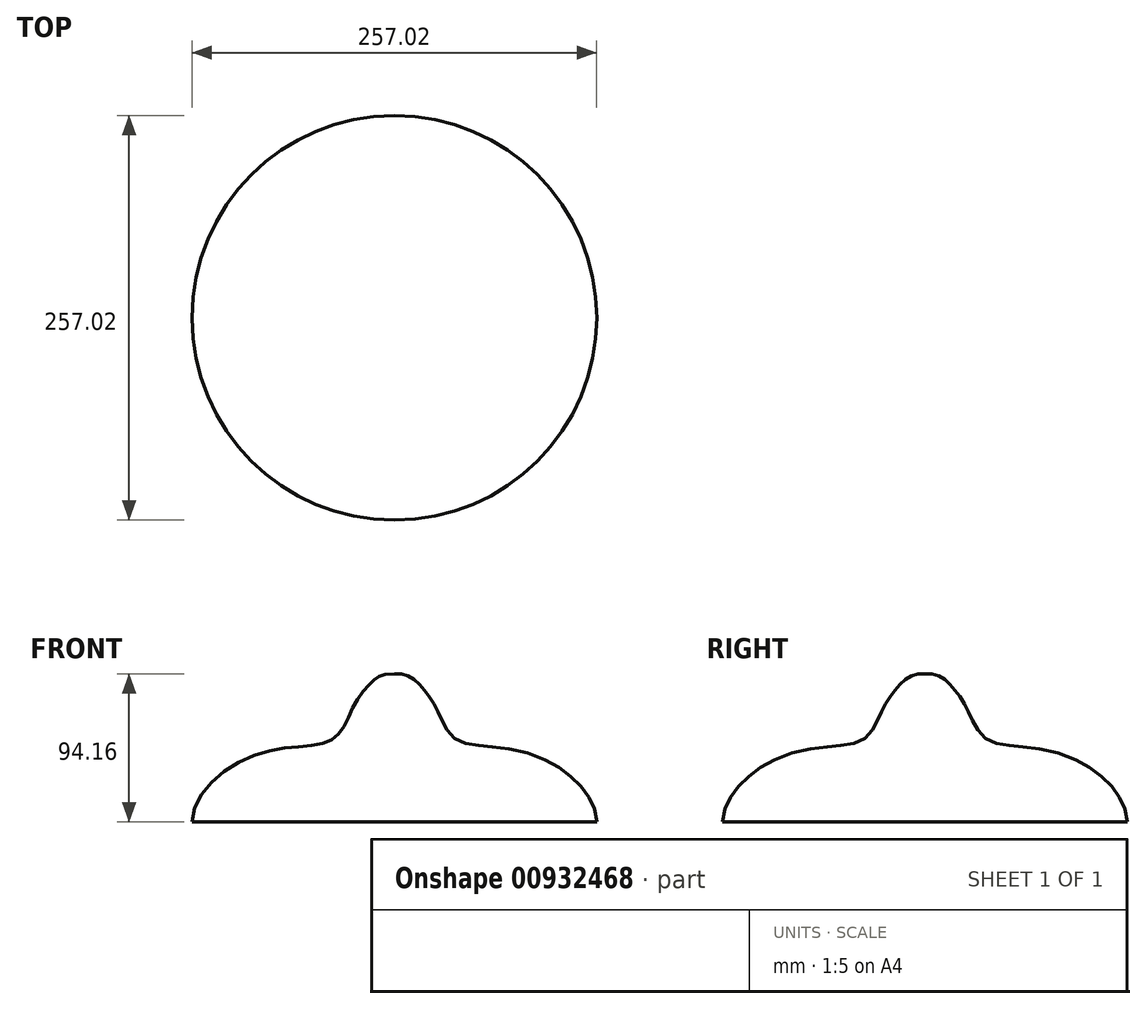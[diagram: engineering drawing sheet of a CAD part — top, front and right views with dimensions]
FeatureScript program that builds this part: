
annotation { "Feature Type Name" : "Feature", "Feature Type Description" : "" }
export const myFeature = defineFeature(function(context is Context, id is Id, definition is map)
    precondition{}
    {
        {
            var Q0;
            Q0=qCreatedBy(makeId("Front.planeOp"),FACE);
            var sketch = newSketch(context, id + "F0", { "sketchPlane" : qUnion([Q0])});
            skLineSegment(sketch, "E0", {"start": v(0, 46.96) * mm, "end": v(0, -47.2) * mm});
            skLineSegment(sketch, "E1", {"start": v(0, -47.2) * mm, "end": v(-128.51, -47.2) * mm});
            skFitSpline(sketch, "E2", {"points": [v(-128.51, -47.2) * mm, v(-84.33, -3.3) * mm, v(-39.47, 5.08) * mm, v(-26, 26.02) * mm, v(-12.82, 43.05) * mm, v(0, 46.96) * mm], "startDerivative": vector(4.7, 208.43) * mm, "endDerivative": vector(166.49, 5.13) * mm});
            skSolve(sketch);
        }
        {
            var Q0;
            Q0=makeQuery(id+"F0.imprint","IMPRINT",FACE,{"disambiguationData":[TD([[makeQuery(id+"F0.imprint","IMPRINT",EDGE,{"derivedFrom":sQuery(id+"F0.wireOp",EDGE,"E0")}),-1.0]])]});
            var Q1;
            Q1=sQuery(id+"F0.wireOp",EDGE,"E0");
            revolve(context, id + "F1", {"surfaceOperationType" : NewSurfaceOperationType.NEW, "entities" : qUnion([Q0]), "axis" : qUnion([Q1]), "revolveType" : RevolveType.FULL});
        }
    });
